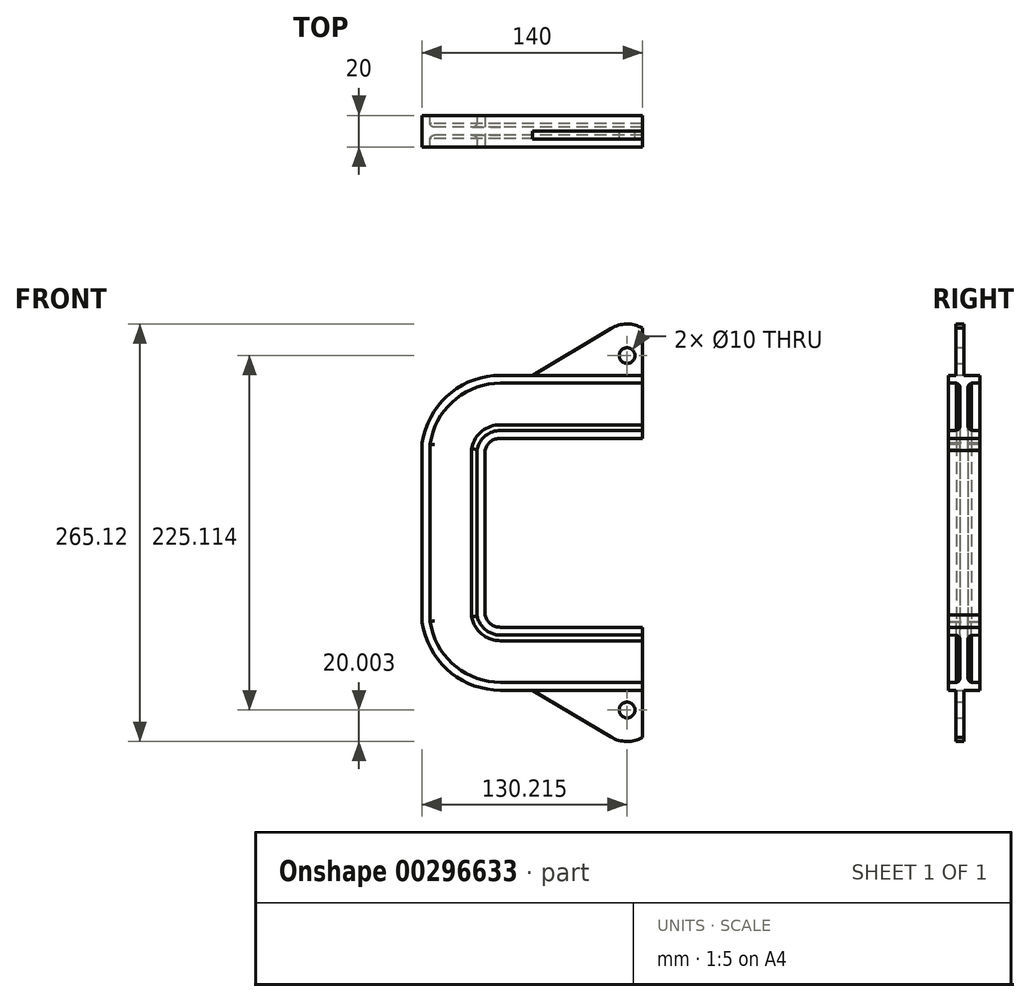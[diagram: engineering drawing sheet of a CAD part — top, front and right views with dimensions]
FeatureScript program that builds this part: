
annotation { "Feature Type Name" : "Feature", "Feature Type Description" : "" }
export const myFeature = defineFeature(function(context is Context, id is Id, definition is map)
    precondition{}
    {
        {
            var Q0;
            Q0=qCreatedBy(makeId("Front.planeOp"),FACE);
            var sketch = newSketch(context, id + "F0", { "sketchPlane" : qUnion([Q0])});
            skLineSegment(sketch, "E0", {"start": v(0, 60) * mm, "end": v(-90.27, 60) * mm});
            skLineSegment(sketch, "E1", {"start": v(-100, 52.3) * mm, "end": v(-100, 0) * mm});
            skArc(sketch, "E2", {"start": v(-90.27, 60) * mm, "mid": v(-96.47, 57.84) * mm, "end": v(-100, 52.3) * mm});
            skSolve(sketch);
        }
        {
            var Q0;
            Q0=qCreatedBy(makeId("Right.planeOp"),FACE);
            var sketch = newSketch(context, id + "F1", { "sketchPlane" : qUnion([Q0])});
            skLineSegment(sketch, "E3", {"start": v(0, 60) * mm, "end": v(10, 60) * mm});
            skArc(sketch, "E4", {"start": v(2.5, 68.58) * mm, "mid": v(3.15, 66.18) * mm, "end": v(5.4, 65.1) * mm});
            skLineSegment(sketch, "E5", {"start": v(2.5, 68.58) * mm, "end": v(2.5, 92.09) * mm});
            skArc(sketch, "E6", {"start": v(4.79, 95) * mm, "mid": v(3.14, 93.94) * mm, "end": v(2.5, 92.09) * mm});
            skLineSegment(sketch, "E7", {"start": v(4.79, 95) * mm, "end": v(10, 95) * mm});
            skLineSegment(sketch, "E8", {"start": v(10, 95) * mm, "end": v(10, 100) * mm});
            skLineSegment(sketch, "E9", {"start": v(10, 100) * mm, "end": v(0, 100) * mm});
            skLineSegment(sketch, "E10.MirrorCS", {"start": v(-4.79, 95) * mm, "end": v(-10, 95) * mm});
            skLineSegment(sketch, "E11.MirrorCS", {"start": v(-10, 95) * mm, "end": v(-10, 100) * mm});
            skArc(sketch, "E12.MirrorCS", {"start": v(-4.79, 95) * mm, "mid": v(-3.14, 93.94) * mm, "end": v(-2.5, 92.09) * mm});
            skArc(sketch, "E13.MirrorCS", {"start": v(-2.5, 68.58) * mm, "mid": v(-3.15, 66.18) * mm, "end": v(-5.4, 65.1) * mm});
            skLineSegment(sketch, "E14.MirrorCS", {"start": v(-10, 100) * mm, "end": v(0, 100) * mm});
            skLineSegment(sketch, "E15.MirrorCS", {"start": v(-2.5, 68.58) * mm, "end": v(-2.5, 92.09) * mm});
            skLineSegment(sketch, "E16", {"start": v(5.4, 65.1) * mm, "end": v(10, 65) * mm});
            skLineSegment(sketch, "E17.MirrorCS", {"start": v(0, 60) * mm, "end": v(-10, 60) * mm});
            skLineSegment(sketch, "E18.MirrorCS", {"start": v(-5.4, 65.1) * mm, "end": v(-10, 65) * mm});
            skLineSegment(sketch, "E19", {"start": v(10, 65) * mm, "end": v(10, 60) * mm});
            skLineSegment(sketch, "E20", {"start": v(-10, 65) * mm, "end": v(-10, 60) * mm});
            skSolve(sketch);
        }
        {
            var Q0;
            Q0=makeQuery(id+"F1.imprint","IMPRINT",FACE,{"disambiguationData":[TD([[makeQuery(id+"F1.imprint","IMPRINT",EDGE,{"derivedFrom":sQuery(id+"F1.wireOp",EDGE,"E3")}),1.0]])]});
            var Q1;
            Q1=sQuery(id+"F0.wireOp",EDGE,"E0");
            var Q2;
            Q2=sQuery(id+"F0.wireOp",EDGE,"E2");
            var Q3;
            Q3=sQuery(id+"F0.wireOp",EDGE,"E1");
            sweep(context, id + "F2", {"profiles" : qUnion([Q0]), "path" : qUnion([Q1, Q2, Q3])});
        }
        {
            var Q0;
            Q0=makeQuery(id+"F2.opSweep","SWEPT_BODY",BODY,{"disambiguationData":[OSD([sQuery(id+"F0.wireOp",EDGE,"E1"),sQuery(id+"F1.wireOp",EDGE,"E3"),sQuery(id+"F1.wireOp",EDGE,"E4"),sQuery(id+"F1.wireOp",EDGE,"E5"),sQuery(id+"F1.wireOp",EDGE,"E6"),sQuery(id+"F1.wireOp",EDGE,"E7"),sQuery(id+"F1.wireOp",EDGE,"E8"),sQuery(id+"F1.wireOp",EDGE,"E9"),sQuery(id+"F1.wireOp",EDGE,"E10.MirrorCS"),sQuery(id+"F1.wireOp",EDGE,"E11.MirrorCS"),sQuery(id+"F1.wireOp",EDGE,"E12.MirrorCS"),sQuery(id+"F1.wireOp",EDGE,"E13.MirrorCS"),sQuery(id+"F1.wireOp",EDGE,"E14.MirrorCS"),sQuery(id+"F1.wireOp",EDGE,"E15.MirrorCS"),sQuery(id+"F1.wireOp",EDGE,"E16"),sQuery(id+"F1.wireOp",EDGE,"E17.MirrorCS"),sQuery(id+"F1.wireOp",EDGE,"E18.MirrorCS"),sQuery(id+"F1.wireOp",EDGE,"E19"),sQuery(id+"F1.wireOp",EDGE,"E20")])]});
            var Q1;
            Q1=qCreatedBy(makeId("Top.planeOp"),FACE);
            mirror(context, id + "F3", {"operationType" : NewBodyOperationType.ADD, "entities" : qUnion([Q0]), "mirrorPlane" : qUnion([Q1])});
        }
        {
            var Q0;
            Q0=qCreatedBy(makeId("Front.planeOp"),FACE);
            var sketch = newSketch(context, id + "F4", { "sketchPlane" : qUnion([Q0])});
            skLineSegment(sketch, "E21", {"start": v(0, -100) * mm, "end": v(-70, -100) * mm});
            skLineSegment(sketch, "E22", {"start": v(-70, -100) * mm, "end": v(-20.01, -129.74) * mm});
            skLineSegment(sketch, "E23", {"start": v(0, -100) * mm, "end": v(0, -130) * mm});
            skArc(sketch, "E24", {"start": v(-20.01, -129.74) * mm, "mid": v(-10.04, -132.56) * mm, "end": v(0, -130) * mm});
            skCircle(sketch, "E25", {"center": v(-9.78, -112.56) * mm, "radius": 5 * mm});
            skCircle(sketch, "E26.MirrorC", {"center": v(-9.78, 112.56) * mm, "radius": 5 * mm});
            skArc(sketch, "E27.MirrorCS", {"start": v(-20.01, 129.74) * mm, "mid": v(-10.04, 132.56) * mm, "end": v(0, 130) * mm});
            skLineSegment(sketch, "E28.MirrorCS", {"start": v(-70, 100) * mm, "end": v(-20.01, 129.74) * mm});
            skLineSegment(sketch, "E29.MirrorCS", {"start": v(0, 100) * mm, "end": v(0, 130) * mm});
            skLineSegment(sketch, "E30.MirrorCS", {"start": v(0, 100) * mm, "end": v(-70, 100) * mm});
            skSolve(sketch);
        }
        {
            var Q0;
            Q0 = qSketchRegion(id + "F4", true);
            extrude(context, id + "F5", {"entities" : qUnion([Q0]), "operationType" : NewBodyOperationType.ADD, "depth" : 5 * mm});
        }
    });
